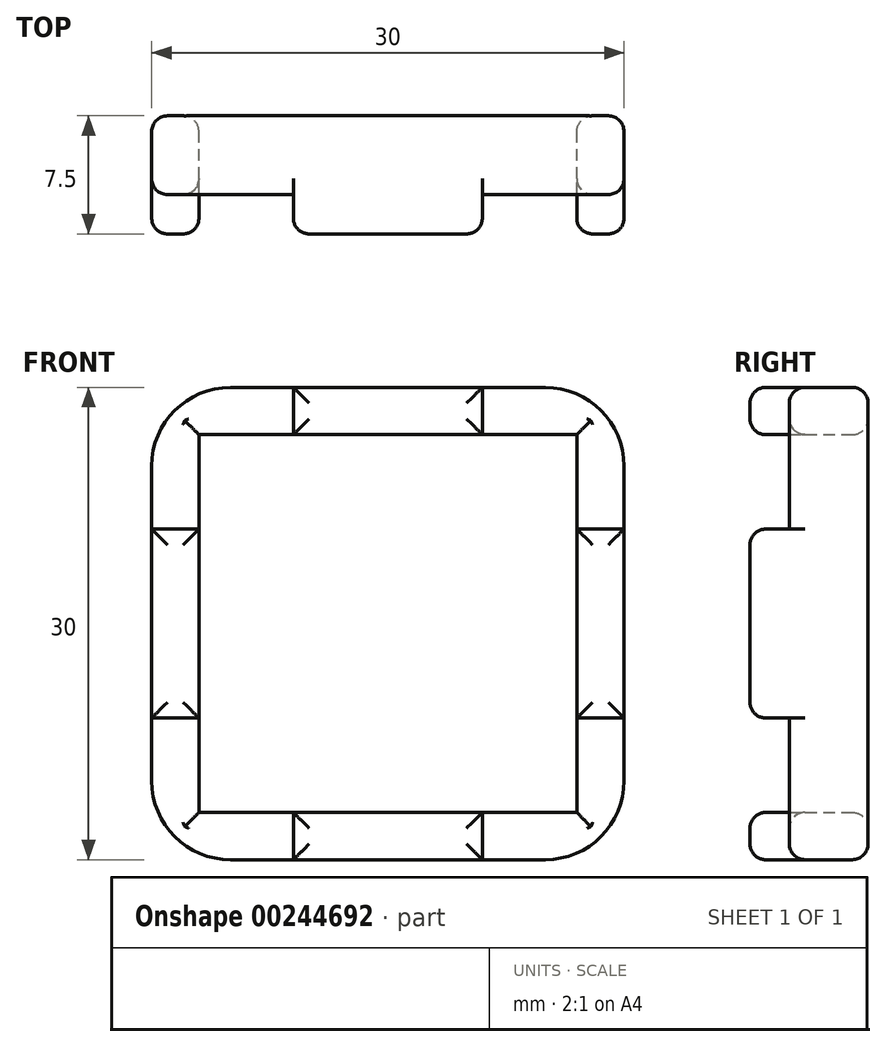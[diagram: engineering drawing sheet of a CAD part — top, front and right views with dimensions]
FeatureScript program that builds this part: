
annotation { "Feature Type Name" : "Feature", "Feature Type Description" : "" }
export const myFeature = defineFeature(function(context is Context, id is Id, definition is map)
    precondition{}
    {
        {
            var Q0;
            Q0=qCreatedBy(makeId("Front.planeOp"),FACE);
            var sketch = newSketch(context, id + "F0", { "sketchPlane" : qUnion([Q0])});
            skLineSegment(sketch, "E0.bottom", {"start": v(15, 15) * mm, "end": v(-15, 15) * mm});
            skLineSegment(sketch, "E0.top", {"start": v(15, -15) * mm, "end": v(-15, -15) * mm});
            skLineSegment(sketch, "E0.left", {"start": v(15, 15) * mm, "end": v(15, -15) * mm});
            skLineSegment(sketch, "E0.right", {"start": v(-15, 15) * mm, "end": v(-15, -15) * mm});
            skPoint(sketch, "E0.middle", {"position": v(0, 0) * mm});
            skLineSegment(sketch, "E1.bottom", {"start": v(12, 12) * mm, "end": v(-12, 12) * mm});
            skLineSegment(sketch, "E1.top", {"start": v(12, -12) * mm, "end": v(-12, -12) * mm});
            skLineSegment(sketch, "E1.left", {"start": v(12, 12) * mm, "end": v(12, -12) * mm});
            skLineSegment(sketch, "E1.right", {"start": v(-12, 12) * mm, "end": v(-12, -12) * mm});
            skPoint(sketch, "E2", {"position": v(-15, 0) * mm});
            skPoint(sketch, "E3", {"position": v(-12, 0) * mm});
            skPoint(sketch, "E4", {"position": v(12, 0) * mm});
            skPoint(sketch, "E5", {"position": v(15, 0) * mm});
            skPoint(sketch, "E6", {"position": v(0, -12) * mm});
            skPoint(sketch, "E7", {"position": v(0, -15) * mm});
            skPoint(sketch, "E8", {"position": v(0, 12) * mm});
            skPoint(sketch, "E9", {"position": v(0, 15) * mm});
            skLineSegment(sketch, "E10", {"start": v(-15, 0) * mm, "end": v(-12, 0) * mm});
            skLineSegment(sketch, "E11", {"start": v(0, -12) * mm, "end": v(0, -15) * mm});
            skLineSegment(sketch, "E12", {"start": v(12, 0) * mm, "end": v(15, 0) * mm});
            skLineSegment(sketch, "E13", {"start": v(0, 12) * mm, "end": v(0, 15) * mm});
            skPoint(sketch, "E14", {"position": v(0, 13.5) * mm});
            skPoint(sketch, "E15", {"position": v(13.5, 0) * mm});
            skPoint(sketch, "E16", {"position": v(0, -13.5) * mm});
            skPoint(sketch, "E17", {"position": v(-13.5, 0) * mm});
            skSolve(sketch);
        }
        {
            var Q0;
            {var subQ3=sQuery(id+"F0.wireOp",EDGE,"E12");Q0=makeQuery(id+"F0.imprint","IMPRINT",FACE,{"disambiguationData":[TD([[makeQuery(id+"F0.imprint","IMPRINT",EDGE,{"derivedFrom":subQ3}),1.0]])]});}
            var Q1;
            {var subQ4=sQuery(id+"F0.wireOp",EDGE,"E11");Q1=makeQuery(id+"F0.imprint","IMPRINT",FACE,{"disambiguationData":[TD([[makeQuery(id+"F0.imprint","IMPRINT",EDGE,{"derivedFrom":subQ4}),1.0]])]});}
            var Q2;
            {var subQ3=sQuery(id+"F0.wireOp",EDGE,"E10");Q2=makeQuery(id+"F0.imprint","IMPRINT",FACE,{"disambiguationData":[TD([[makeQuery(id+"F0.imprint","IMPRINT",EDGE,{"derivedFrom":subQ3}),-1.0]])]});}
            var Q3;
            {var subQ3=sQuery(id+"F0.wireOp",EDGE,"E10");Q3=makeQuery(id+"F0.imprint","IMPRINT",FACE,{"disambiguationData":[TD([[makeQuery(id+"F0.imprint","IMPRINT",EDGE,{"derivedFrom":subQ3}),1.0]])]});}
            var Q4;
            Q4 = qSketchRegion(id + "F2", true);
            extrude(context, id + "F1", {"entities" : qUnion([Q0, Q1, Q2, Q3, Q4]), "endBound" : BoundingType.SYMMETRIC, "depth" : 5 * mm});
        }
        {
            var Q0;
            Q0=makeQuery(id+"F1.opExtrude","CAP_FACE",FACE,{"disambiguationData":[OSD([sQuery(id+"F0.wireOp",EDGE,"E0.bottom"),sQuery(id+"F0.wireOp",EDGE,"E0.top"),sQuery(id+"F0.wireOp",EDGE,"E0.left"),sQuery(id+"F0.wireOp",EDGE,"E0.right"),sQuery(id+"F0.wireOp",EDGE,"E1.bottom"),sQuery(id+"F0.wireOp",EDGE,"E1.top"),sQuery(id+"F0.wireOp",EDGE,"E1.left"),sQuery(id+"F0.wireOp",EDGE,"E1.right")])],"isStart":false});
            var sketch = newSketch(context, id + "F2", { "sketchPlane" : qUnion([Q0])});
            skPoint(sketch, "E18", {"position": v(-13.5, 0) * mm});
            skPoint(sketch, "E19", {"position": v(13.5, 0) * mm});
            skPoint(sketch, "E20", {"position": v(0, 13.5) * mm});
            skPoint(sketch, "E21", {"position": v(0, -13.5) * mm});
            skPoint(sketch, "E21.positionSnap0", {"position": v(0, -12) * mm});
            skLineSegment(sketch, "E22.bottom", {"start": v(-12, 6) * mm, "end": v(-15, 6) * mm});
            skLineSegment(sketch, "E22.top", {"start": v(-12, -6) * mm, "end": v(-15, -6) * mm});
            skLineSegment(sketch, "E22.left", {"start": v(-12, 6) * mm, "end": v(-12, -6) * mm});
            skLineSegment(sketch, "E22.right", {"start": v(-15, 6) * mm, "end": v(-15, -6) * mm});
            skLineSegment(sketch, "E23.bottom", {"start": v(6, -12) * mm, "end": v(-6, -12) * mm});
            skLineSegment(sketch, "E23.top", {"start": v(6, -15) * mm, "end": v(-6, -15) * mm});
            skLineSegment(sketch, "E23.left", {"start": v(6, -12) * mm, "end": v(6, -15) * mm});
            skLineSegment(sketch, "E23.right", {"start": v(-6, -12) * mm, "end": v(-6, -15) * mm});
            skLineSegment(sketch, "E24.bottom", {"start": v(15, 6) * mm, "end": v(12, 6) * mm});
            skLineSegment(sketch, "E24.top", {"start": v(15, -6) * mm, "end": v(12, -6) * mm});
            skLineSegment(sketch, "E24.left", {"start": v(15, 6) * mm, "end": v(15, -6) * mm});
            skLineSegment(sketch, "E24.right", {"start": v(12, 6) * mm, "end": v(12, -6) * mm});
            skLineSegment(sketch, "E25.bottom", {"start": v(6, 15) * mm, "end": v(-6, 15) * mm});
            skLineSegment(sketch, "E25.top", {"start": v(6, 12) * mm, "end": v(-6, 12) * mm});
            skLineSegment(sketch, "E25.left", {"start": v(6, 15) * mm, "end": v(6, 12) * mm});
            skLineSegment(sketch, "E25.right", {"start": v(-6, 15) * mm, "end": v(-6, 12) * mm});
            skSolve(sketch);
        }
        {
            var Q0;
            Q0=makeQuery(id+"F2.imprint","IMPRINT",FACE,{"disambiguationData":[TD([[makeQuery(id+"F2.imprint","IMPRINT",EDGE,{"derivedFrom":sQuery(id+"F2.wireOp",EDGE,"E25.bottom")}),1.0]])]});
            var Q1;
            Q1=makeQuery(id+"F2.imprint","IMPRINT",FACE,{"disambiguationData":[TD([[makeQuery(id+"F2.imprint","IMPRINT",EDGE,{"derivedFrom":sQuery(id+"F2.wireOp",EDGE,"E24.bottom")}),1.0]])]});
            var Q2;
            Q2=makeQuery(id+"F2.imprint","IMPRINT",FACE,{"disambiguationData":[TD([[makeQuery(id+"F2.imprint","IMPRINT",EDGE,{"derivedFrom":sQuery(id+"F2.wireOp",EDGE,"E23.bottom")}),1.0]])]});
            var Q3;
            {var subQ0=sQuery(id+"F2.wireOp",EDGE,"E22.left");Q3=makeQuery(id+"F2.imprint","IMPRINT",FACE,{"disambiguationData":[TD([[makeQuery(id+"F2.imprint","IMPRINT",EDGE,{"derivedFrom":subQ0}),-1.0]])]});}
            extrude(context, id + "F3", {"entities" : qUnion([Q0, Q1, Q2, Q3]), "operationType" : NewBodyOperationType.ADD, "depth" : 2.5 * mm});
        }
        {
            var Q0;
            Q0=makeQuery(id+"F1.opExtrude","SWEPT_EDGE",EDGE,{"disambiguationData":[OSD([sQuery(id+"F0.wireOp",EDGE,"E0.bottom"),sQuery(id+"F0.wireOp",EDGE,"E0.right")])]});
            var Q1;
            Q1=makeQuery(id+"F1.opExtrude","SWEPT_EDGE",EDGE,{"disambiguationData":[OSD([sQuery(id+"F0.wireOp",EDGE,"E0.top"),sQuery(id+"F0.wireOp",EDGE,"E0.right")])]});
            var Q2;
            Q2=makeQuery(id+"F1.opExtrude","SWEPT_EDGE",EDGE,{"disambiguationData":[OSD([sQuery(id+"F0.wireOp",EDGE,"E0.bottom"),sQuery(id+"F0.wireOp",EDGE,"E0.left")])]});
            var Q3;
            Q3=makeQuery(id+"F1.opExtrude","SWEPT_EDGE",EDGE,{"disambiguationData":[OSD([sQuery(id+"F0.wireOp",EDGE,"E0.top"),sQuery(id+"F0.wireOp",EDGE,"E0.left")])]});
            fillet(context, id + "F4", {"entities" : qUnion([Q0, Q1, Q2, Q3]), "radius" : 5 * mm, "tangentPropagation" : true, "allowEdgeOverflow" : false});
        }
        {
            var Q0;
            Q0=makeQuery(id+"F3.opExtrude","CAP_FACE",FACE,{"disambiguationData":[OSD([sQuery(id+"F0.wireOp",EDGE,"E1.bottom"),sQuery(id+"FwlsijgZc56MNb0_1.wireOp",EDGE,"nSc84qVd-UhBY-GhX5-03Qc-sTRTGPTtrw4R.bottom"),sQuery(id+"FwlsijgZc56MNb0_1.wireOp",EDGE,"nSc84qVd-UhBY-GhX5-03Qc-sTRTGPTtrw4R.left"),sQuery(id+"FwlsijgZc56MNb0_1.wireOp",EDGE,"nSc84qVd-UhBY-GhX5-03Qc-sTRTGPTtrw4R.right")])],"isStart":false});
            var Q1;
            Q1=makeQuery(id+"F3.opExtrude","CAP_FACE",FACE,{"disambiguationData":[OSD([sQuery(id+"F0.wireOp",EDGE,"E0.right"),sQuery(id+"FwlsijgZc56MNb0_1.wireOp",EDGE,"JnJIatAS-PfJz-8yNd-gNbl-uyd0QJJkPRL4.bottom"),sQuery(id+"FwlsijgZc56MNb0_1.wireOp",EDGE,"JnJIatAS-PfJz-8yNd-gNbl-uyd0QJJkPRL4.top"),sQuery(id+"FwlsijgZc56MNb0_1.wireOp",EDGE,"JnJIatAS-PfJz-8yNd-gNbl-uyd0QJJkPRL4.left")])],"isStart":false});
            var Q2;
            Q2=makeQuery(id+"F3.opExtrude","CAP_FACE",FACE,{"disambiguationData":[OSD([sQuery(id+"F0.wireOp",EDGE,"E1.top"),sQuery(id+"FwlsijgZc56MNb0_1.wireOp",EDGE,"1sdIi1DR-BB7f-S7uz-lD4y-kShEhdNSRRUE.top"),sQuery(id+"FwlsijgZc56MNb0_1.wireOp",EDGE,"1sdIi1DR-BB7f-S7uz-lD4y-kShEhdNSRRUE.left"),sQuery(id+"FwlsijgZc56MNb0_1.wireOp",EDGE,"1sdIi1DR-BB7f-S7uz-lD4y-kShEhdNSRRUE.right")])],"isStart":false});
            var Q3;
            Q3=makeQuery(id+"F3.opExtrude","CAP_FACE",FACE,{"disambiguationData":[OSD([sQuery(id+"F0.wireOp",EDGE,"E1.left"),sQuery(id+"FwlsijgZc56MNb0_1.wireOp",EDGE,"n3T7m2Pr-l0Dm-tZDm-wsku-B2I1hSbsFz1c.bottom"),sQuery(id+"FwlsijgZc56MNb0_1.wireOp",EDGE,"n3T7m2Pr-l0Dm-tZDm-wsku-B2I1hSbsFz1c.top"),sQuery(id+"FwlsijgZc56MNb0_1.wireOp",EDGE,"n3T7m2Pr-l0Dm-tZDm-wsku-B2I1hSbsFz1c.left")])],"isStart":false});
            var Q4;
            Q4=makeQuery(id+"F1.opExtrude","CAP_EDGE",EDGE,{"disambiguationData":[OSD([sQuery(id+"F0.wireOp",EDGE,"E0.right")])],"isStart":true});
            var Q5;
            Q5=makeQuery(id+"F1.opExtrude","CAP_EDGE",EDGE,{"disambiguationData":[OSD([sQuery(id+"F0.wireOp",EDGE,"E1.right")])],"isStart":true});
            var Q6;
            Q6=makeQuery(id+"F1.opExtrude","CAP_EDGE",EDGE,{"disambiguationData":[OSD([sQuery(id+"F0.wireOp",EDGE,"E1.bottom")])],"isStart":true});
            var Q7;
            Q7=makeQuery(id+"F1.opExtrude","CAP_EDGE",EDGE,{"disambiguationData":[OSD([sQuery(id+"F0.wireOp",EDGE,"E1.left")])],"isStart":true});
            var Q8;
            Q8=makeQuery(id+"F1.opExtrude","CAP_EDGE",EDGE,{"disambiguationData":[OSD([sQuery(id+"F0.wireOp",EDGE,"E1.top")])],"isStart":true});
            var Q9;
            {var subQ0=sQuery(id+"F0.wireOp",EDGE,"E1.right");var subQ1=sQuery(id+"F0.wireOp",EDGE,"E1.bottom");Q9=makeQuery(id+"F3.boolean.opBoolean","SPLIT",EDGE,{"disambiguationData":[TD([makeQuery(id+"F1.opExtrude","SWEPT_FACE",FACE,{"disambiguationData":[OSD([subQ0])]})])],"derivedFrom":makeQuery(id+"F1.opExtrude","CAP_EDGE",EDGE,{"disambiguationData":[OSD([subQ1])],"isStart":false})});}
            var Q10;
            {var subQ0=sQuery(id+"F0.wireOp",EDGE,"E1.bottom");var subQ1=sQuery(id+"F0.wireOp",EDGE,"E1.left");Q10=makeQuery(id+"F3.boolean.opBoolean","SPLIT",EDGE,{"disambiguationData":[TD([makeQuery(id+"F1.opExtrude","SWEPT_FACE",FACE,{"disambiguationData":[OSD([subQ1])]})])],"derivedFrom":makeQuery(id+"F1.opExtrude","CAP_EDGE",EDGE,{"disambiguationData":[OSD([subQ0])],"isStart":false})});}
            var Q11;
            {var subQ0=sQuery(id+"F0.wireOp",EDGE,"E0.left");var subQ1=sQuery(id+"F0.wireOp",EDGE,"E0.bottom");Q11=makeQuery(id+"F3.boolean.opBoolean","SPLIT",EDGE,{"disambiguationData":[TD([makeQuery(id+"F1.opExtrude","SWEPT_FACE",FACE,{"disambiguationData":[OSD([subQ0])]})])],"derivedFrom":makeQuery(id+"F1.opExtrude","CAP_EDGE",EDGE,{"disambiguationData":[OSD([subQ1])],"isStart":false})});}
            var Q12;
            {var subQ0=sQuery(id+"F0.wireOp",EDGE,"E0.right");var subQ1=sQuery(id+"F0.wireOp",EDGE,"E0.bottom");Q12=makeQuery(id+"F3.boolean.opBoolean","SPLIT",EDGE,{"disambiguationData":[TD([makeQuery(id+"F1.opExtrude","SWEPT_FACE",FACE,{"disambiguationData":[OSD([subQ0])]})])],"derivedFrom":makeQuery(id+"F1.opExtrude","CAP_EDGE",EDGE,{"disambiguationData":[OSD([subQ1])],"isStart":false})});}
            var Q13;
            {var subQ0=sQuery(id+"F0.wireOp",EDGE,"E1.bottom");var subQ1=sQuery(id+"F0.wireOp",EDGE,"E1.right");Q13=makeQuery(id+"F3.boolean.opBoolean","SPLIT",EDGE,{"disambiguationData":[TD([makeQuery(id+"F1.opExtrude","SWEPT_FACE",FACE,{"disambiguationData":[OSD([subQ0])]})])],"derivedFrom":makeQuery(id+"F1.opExtrude","CAP_EDGE",EDGE,{"disambiguationData":[OSD([subQ1])],"isStart":false})});}
            var Q14;
            {var subQ0=sQuery(id+"F0.wireOp",EDGE,"E1.top");var subQ1=sQuery(id+"F0.wireOp",EDGE,"E1.right");Q14=makeQuery(id+"F3.boolean.opBoolean","SPLIT",EDGE,{"disambiguationData":[TD([makeQuery(id+"F1.opExtrude","SWEPT_FACE",FACE,{"disambiguationData":[OSD([subQ0])]})])],"derivedFrom":makeQuery(id+"F1.opExtrude","CAP_EDGE",EDGE,{"disambiguationData":[OSD([subQ1])],"isStart":false})});}
            var Q15;
            {var subQ0=sQuery(id+"F0.wireOp",EDGE,"E1.top");var subQ1=sQuery(id+"F0.wireOp",EDGE,"E1.right");Q15=makeQuery(id+"F3.boolean.opBoolean","SPLIT",EDGE,{"disambiguationData":[TD([makeQuery(id+"F1.opExtrude","SWEPT_FACE",FACE,{"disambiguationData":[OSD([subQ1])]})])],"derivedFrom":makeQuery(id+"F1.opExtrude","CAP_EDGE",EDGE,{"disambiguationData":[OSD([subQ0])],"isStart":false})});}
            var Q16;
            {var subQ0=sQuery(id+"F0.wireOp",EDGE,"E1.top");var subQ1=sQuery(id+"F0.wireOp",EDGE,"E1.left");Q16=makeQuery(id+"F3.boolean.opBoolean","SPLIT",EDGE,{"disambiguationData":[TD([makeQuery(id+"F1.opExtrude","SWEPT_FACE",FACE,{"disambiguationData":[OSD([subQ1])]})])],"derivedFrom":makeQuery(id+"F1.opExtrude","CAP_EDGE",EDGE,{"disambiguationData":[OSD([subQ0])],"isStart":false})});}
            var Q17;
            {var subQ0=sQuery(id+"F0.wireOp",EDGE,"E1.top");var subQ1=sQuery(id+"F0.wireOp",EDGE,"E1.left");Q17=makeQuery(id+"F3.boolean.opBoolean","SPLIT",EDGE,{"disambiguationData":[TD([makeQuery(id+"F1.opExtrude","SWEPT_FACE",FACE,{"disambiguationData":[OSD([subQ0])]})])],"derivedFrom":makeQuery(id+"F1.opExtrude","CAP_EDGE",EDGE,{"disambiguationData":[OSD([subQ1])],"isStart":false})});}
            var Q18;
            {var subQ0=sQuery(id+"F0.wireOp",EDGE,"E0.right");var subQ1=sQuery(id+"F0.wireOp",EDGE,"E0.top");Q18=makeQuery(id+"F3.boolean.opBoolean","SPLIT",EDGE,{"disambiguationData":[TD([makeQuery(id+"F1.opExtrude","SWEPT_FACE",FACE,{"disambiguationData":[OSD([subQ0])]})])],"derivedFrom":makeQuery(id+"F1.opExtrude","CAP_EDGE",EDGE,{"disambiguationData":[OSD([subQ1])],"isStart":false})});}
            var Q19;
            {var subQ0=sQuery(id+"F0.wireOp",EDGE,"E0.left");var subQ1=sQuery(id+"F0.wireOp",EDGE,"E0.top");Q19=makeQuery(id+"F3.boolean.opBoolean","SPLIT",EDGE,{"disambiguationData":[TD([makeQuery(id+"F1.opExtrude","SWEPT_FACE",FACE,{"disambiguationData":[OSD([subQ0])]})])],"derivedFrom":makeQuery(id+"F1.opExtrude","CAP_EDGE",EDGE,{"disambiguationData":[OSD([subQ1])],"isStart":false})});}
            var Q20;
            {var subQ0=sQuery(id+"F0.wireOp",EDGE,"E1.bottom");var subQ1=sQuery(id+"F0.wireOp",EDGE,"E1.left");Q20=makeQuery(id+"F3.boolean.opBoolean","SPLIT",EDGE,{"disambiguationData":[TD([makeQuery(id+"F1.opExtrude","SWEPT_FACE",FACE,{"disambiguationData":[OSD([subQ0])]})])],"derivedFrom":makeQuery(id+"F1.opExtrude","CAP_EDGE",EDGE,{"disambiguationData":[OSD([subQ1])],"isStart":false})});}
            var Q21;
            Q21=makeQuery(id+"F3.opExtrude","CAP_FACE",FACE,{"disambiguationData":[OSD([sQuery(id+"F2.wireOp",EDGE,"E23.bottom"),sQuery(id+"F2.wireOp",EDGE,"E23.top"),sQuery(id+"F2.wireOp",EDGE,"E23.left"),sQuery(id+"F2.wireOp",EDGE,"E23.right")])],"isStart":false});
            var Q22;
            Q22=makeQuery(id+"F3.opExtrude","CAP_FACE",FACE,{"disambiguationData":[OSD([sQuery(id+"F2.wireOp",EDGE,"E24.bottom"),sQuery(id+"F2.wireOp",EDGE,"E24.top"),sQuery(id+"F2.wireOp",EDGE,"E24.left"),sQuery(id+"F2.wireOp",EDGE,"E24.right")])],"isStart":false});
            var Q23;
            Q23=makeQuery(id+"F3.opExtrude","CAP_EDGE",EDGE,{"disambiguationData":[OSD([sQuery(id+"F2.wireOp",EDGE,"E25.bottom")])],"isStart":false});
            var Q24;
            Q24=makeQuery(id+"F3.opExtrude","CAP_FACE",FACE,{"disambiguationData":[OSD([sQuery(id+"F2.wireOp",EDGE,"E25.bottom"),sQuery(id+"F2.wireOp",EDGE,"E25.top"),sQuery(id+"F2.wireOp",EDGE,"E25.left"),sQuery(id+"F2.wireOp",EDGE,"E25.right")])],"isStart":false});
            fillet(context, id + "F5", {"entities" : qUnion([Q0, Q1, Q2, Q3, Q4, Q5, Q6, Q7, Q8, Q9, Q10, Q11, Q12, Q13, Q14, Q15, Q16, Q17, Q18, Q19, Q20, Q21, Q22, Q23, Q24]), "radius" : 1 * mm, "tangentPropagation" : true, "allowEdgeOverflow" : false});
        }
    });
